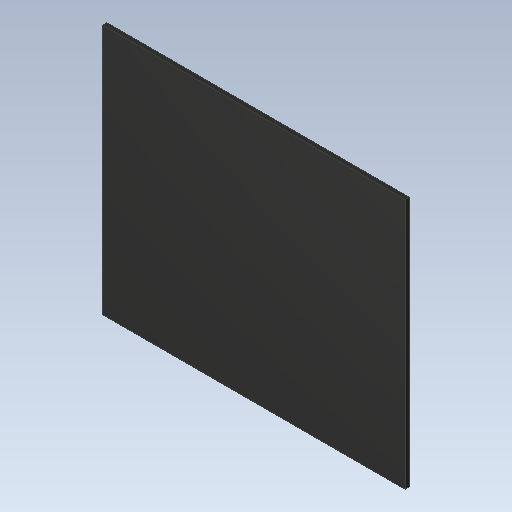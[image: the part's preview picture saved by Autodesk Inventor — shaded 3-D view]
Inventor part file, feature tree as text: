
AUTODESK INVENTOR PART (.ipt)
format: ipt  version: 2020 (Build 240168000, 168)  size: 88,064 bytes
history: imported  units: in
note: dims shown in document units (in); Inventor stores cm internally (conversion verified against a paired STEP export)
features: imported_body x1
ambient origin geometry x8: Origin, YZ Plane, XZ Plane, XY Plane, X Axis, Y Axis, Z Axis, Center Point
bodies: Solid1 (imported_parasolid), Body1 (imported_parasolid)
feature tree (1):
  imported_body  NMx_Import_Brep_tag  [imported B-rep: ~6 faces, bbox_mm=[7.35, 6.1, 0.1]]
